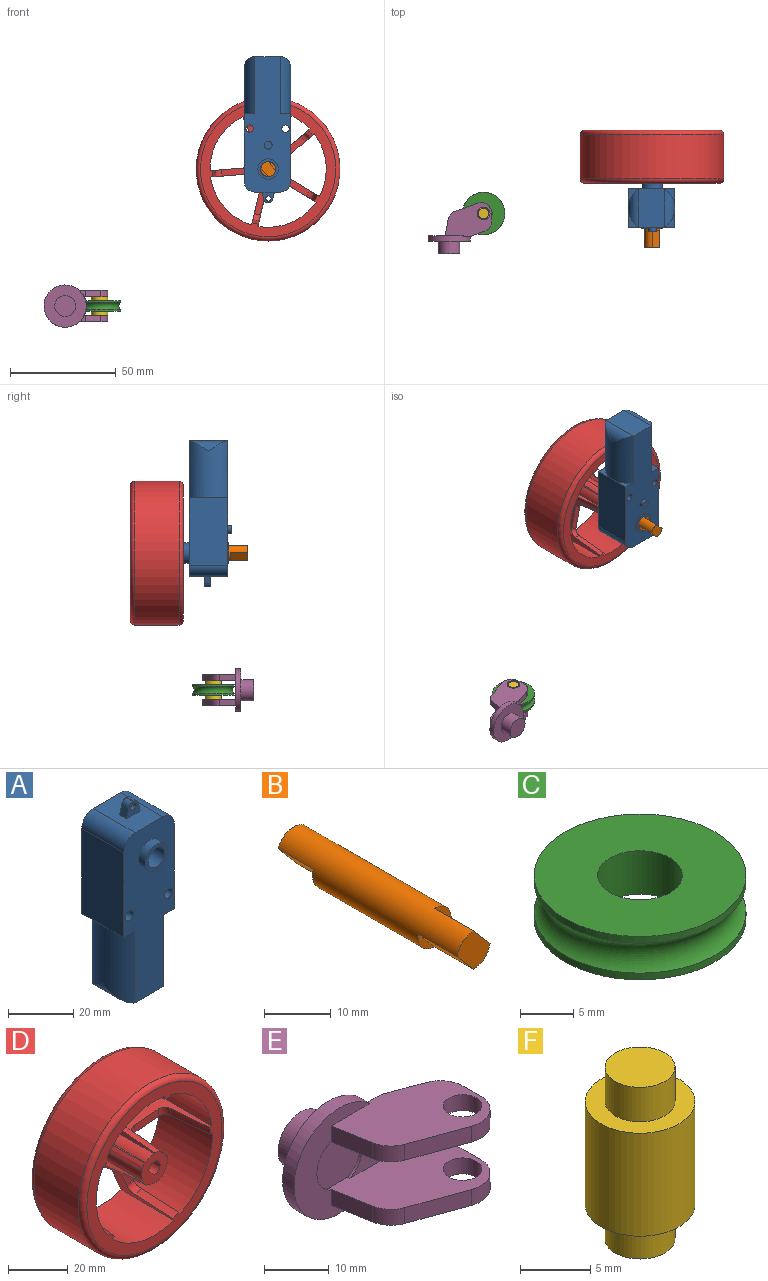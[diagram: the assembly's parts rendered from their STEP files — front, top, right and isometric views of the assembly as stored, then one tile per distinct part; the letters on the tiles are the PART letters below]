
ASSEMBLY  parts=6 mates=4
PART A: 33 faces, bbox 22x23.2x69.1 mm
  f0: plane 32x18.25mm, normal (-1,0,0), area 584mm2, adj f4,f5,f7,f25,f26
  f1: cylinder r=5mm len=18.25mm, axis (0,1,0), area 81.4mm2, adj f4,f5,f8,f24
  f2: cylinder r=5mm len=18.25mm, axis (0,1,0), area 81.4mm2, adj f4,f5,f8,f22
  f3: plane 32x18.25mm, normal (1,0,0), area 584mm2, adj f4,f5,f9,f21,f23
  f4: plane 64x22mm, normal (0,-1,0), area 1041.8mm2, adj f0,f1,f2,f3,f6,f7,f8,f9
  f5: plane 64x22mm, normal (0,1,0), area 1031.1mm2, adj f0,f1,f2,f3,f6,f7,f8,f9
  f6: plane 18.25x12mm, normal (0,0,1), area 201mm2, adj f4,f5,f7,f9,f13,f14,f15,f16
  f7: cylinder r=5mm len=18.25mm, axis (0,1,0), area 143.3mm2, adj f0,f4,f5,f6
  f8: plane 18.25x12mm, normal (0,0,-1), area 219mm2, adj f1,f2,f4,f5
  f9: cylinder r=5mm len=18.25mm, axis (0,1,0), area 143.3mm2, adj f3,f4,f5,f6
  f10: cylinder r=4.85mm len=9.7mm, axis (0,1,0), area 88.4mm2, adj f4,f12
  f11: cylinder r=3.6mm len=21.65mm, axis (0,1,0), area 489.7mm2, adj f12,f28
  f12: plane 9.7x9.7mm, normal (0,-1,0), area 33.2mm2, adj f10,f11
  f13: plane 6x5.1mm, normal (0,-1,0), area 17.8mm2, adj f6,f14,f16,f17,f18,f19,f20
  f14: plane 3.62x3mm, normal (0.97,0,0.26), area 11.2mm2, adj f6,f13,f15,f18
  f15: plane 6x5.1mm, normal (0,1,0), area 17.8mm2, adj f6,f14,f16,f17,f18,f19,f20
  f16: plane 3.62x3mm, normal (-0.97,0,0.26), area 11.2mm2, adj f6,f13,f15,f19
  f17: plane 3x0.2mm, normal (0,0,1), area 0.6mm2, adj f13,f15,f18,f19
  f18: cylinder r=2mm len=3mm, axis (0,1,0), area 7.9mm2, adj f13,f14,f15,f17
  f19: cylinder r=2mm len=3mm, axis (0,1,0), area 7.9mm2, adj f13,f15,f16,f17
  f20: cylinder r=1.25mm len=3mm, axis (0,-1,0), area 23.6mm2, adj f13,f15
  f21: plane 9.13x4.86mm, normal (0,0,-1), area 13.2mm2, adj f3,f5,f22
  f22: cylinder r=11mm len=27mm, axis (0,0,-1), area 539.6mm2, adj f2,f4,f5,f21,f23
  f23: plane 9.13x4.86mm, normal (0,0,-1), area 13.2mm2, adj f3,f4,f22
  f24: cylinder r=11mm len=27mm, axis (0,0,-1), area 539.6mm2, adj f1,f4,f5,f25,f26
  f25: plane 9.13x4.86mm, normal (0,0,-1), area 13.2mm2, adj f0,f5,f24
  f26: plane 9.13x4.86mm, normal (0,0,-1), area 13.2mm2, adj f0,f4,f24
  f27: cylinder r=4.85mm len=9.7mm, axis (0,-1,0), area 15.2mm2, adj f5,f28
  f28: plane 9.7x9.7mm, normal (0,1,0), area 33.2mm2, adj f11,f27
  f29: cylinder r=1.85mm len=3.7mm, axis (0,-1,0), area 23.2mm2, adj f5,f30
  f30: plane 3.7x3.7mm, normal (0,1,0), area 10.8mm2, adj f29
  f31: cylinder r=1.75mm len=18.25mm, axis (0,-1,0), area 200.7mm2, adj f4,f5
  f32: cylinder r=1.75mm len=18.25mm, axis (0,-1,0), area 200.7mm2, adj f4,f5
PART B: 9 faces, bbox 7x38x7 mm
  f0: plane 7x6.93mm, normal (0,-1,0), area 29.7mm2, adj f2,f5,f7
  f1: plane 6.94x6.8mm, normal (0,1,0), area 31mm2, adj f2,f3
  f2: cylinder r=3.5mm len=38mm, axis (0,1,0), area 682.1mm2, adj f0,f1,f3,f4,f5,f6,f7,f8
  f3: plane 7.5x4.6mm, normal (-0.76,0,-0.65), area 45.5mm2, adj f1,f2,f4
  f4: plane 4.66x4.15mm, normal (0,1,0), area 7.5mm2, adj f2,f3
  f5: plane 8.25x4mm, normal (-0.76,0,-0.65), area 43.5mm2, adj f0,f2,f6
  f6: plane 4x3.47mm, normal (0,-1,0), area 4.4mm2, adj f2,f5
  f7: plane 8.25x4mm, normal (0.76,0,0.65), area 43.5mm2, adj f0,f2,f8
  f8: plane 4x3.47mm, normal (0,-1,0), area 4.4mm2, adj f2,f7
PART C: 6 faces, bbox 23.8x23.8x5 mm
  f0: cylinder r=10mm len=20mm, axis (0,0,-1), area 48.3mm2, adj f3,f5
  f1: cylinder r=4mm len=8mm, axis (0,0,-1), area 125.7mm2, adj f3,f4
  f2: cylinder r=10mm len=20mm, axis (0,0,-1), area 48.3mm2, adj f4,f5
  f3: plane 20x20mm, normal (0,0,1), area 263.9mm2, adj f0,f1
  f4: plane 20x20mm, normal (0,0,-1), area 263.9mm2, adj f1,f2
  f5: torus R=11mm, axis (0,0,1), area 246mm2, adj f0,f2
PART D: 53 faces, bbox 73.4x25x73.4 mm
  f0: plane 12.54x12.32mm, normal (0,-1,0), area 97.4mm2, adj f9,f10,f11,f12,f13,f14,f15,f16
  f1: cylinder r=27.5mm len=29.75mm, axis (0,1,0), area 788.9mm2, adj f7,f8,f9,f22
  f2: cylinder r=27.5mm len=29.05mm, axis (0,1,0), area 788.9mm2, adj f7,f8,f10,f12
  f3: cylinder r=27.5mm len=25.5mm, axis (0,1,0), area 788.9mm2, adj f7,f8,f13,f15
  f4: cylinder r=27.5mm len=25mm, axis (0,1,0), area 788.9mm2, adj f7,f8,f16,f18
  f5: cylinder r=27.5mm len=27.55mm, axis (0,1,0), area 788.9mm2, adj f7,f8,f19,f21
  f6: cylinder r=34mm len=68mm, axis (0,1,0), area 4486.2mm2, adj f51,f52
  f7: plane 64x64mm, normal (0,-1,0), area 856.8mm2, adj f1,f2,f3,f4,f5,f9,f10,f12
  f8: plane 64x64mm, normal (0,1,0), area 1257.1mm2, adj f1,f2,f3,f4,f5,f9,f10,f11
  f9: plane 25.04x16.46mm, normal (-0.65,0,0.76), area 174.1mm2, adj f0,f1,f7,f8,f25,f46,f47,f48
  f10: plane 25.04x16.46mm, normal (0.65,0,-0.76), area 174.1mm2, adj f0,f2,f7,f8,f11,f46,f47,f48
  f11: cylinder r=6mm len=25mm, axis (0,1,0), area 112.7mm2, adj f0,f8,f10,f12
  f12: plane 25.04x20.01mm, normal (-0.92,0,-0.39), area 174.1mm2, adj f0,f2,f7,f8,f11,f41,f42,f43
  f13: plane 25.04x20.01mm, normal (0.92,0,0.39), area 174.1mm2, adj f0,f3,f7,f8,f14,f41,f42,f43
  f14: cylinder r=6mm len=25mm, axis (0,1,0), area 112.7mm2, adj f0,f8,f13,f15
  f15: plane 25.04x21.61mm, normal (0.08,0,-1), area 174.1mm2, adj f0,f3,f7,f8,f14,f36,f37,f38
  f16: plane 25.04x21.61mm, normal (-0.08,0,1), area 174.1mm2, adj f0,f4,f7,f8,f17,f36,f37,f38
  f17: cylinder r=6mm len=25mm, axis (0,1,0), area 112.7mm2, adj f0,f8,f16,f18
  f18: plane 25.04x21.1mm, normal (0.97,0,-0.23), area 174.1mm2, adj f0,f4,f7,f8,f17,f31,f32,f33
  f19: plane 25.04x21.1mm, normal (-0.97,0,0.23), area 174.1mm2, adj f0,f5,f7,f8,f20,f31,f32,f33
  f20: cylinder r=6mm len=25mm, axis (0,1,0), area 112.7mm2, adj f0,f8,f19,f21
  f21: plane 25.04x18.53mm, normal (0.52,0,0.85), area 174.1mm2, adj f0,f5,f7,f8,f20,f26,f27,f28
  f22: plane 25.04x18.53mm, normal (-0.52,0,-0.85), area 174.1mm2, adj f0,f1,f7,f8,f25,f26,f27,f28
  f23: cylinder r=2.7mm len=25mm, axis (0,1,0), area 310.6mm2, adj f0,f8,f24
  f24: plane 25x3.05mm, normal (0.76,0,0.65), area 100.6mm2, adj f0,f8,f23
  f25: cylinder r=6mm len=25mm, axis (0,1,0), area 112.7mm2, adj f0,f8,f9,f22
  f26: cone r=26.46mm half-angle=5deg, axis (0,-1,0), area 52mm2, adj f7,f21,f22,f27
  f27: torus R=21.96mm, axis (0,-1,0), area 13.4mm2, adj f21,f22,f26,f28
  f28: plane 11.13x8.39mm, normal (0,-1,0), area 33.5mm2, adj f21,f22,f27,f29
  f29: torus R=10.81mm, axis (0,-1,0), area 13.4mm2, adj f21,f22,f28,f30
  f30: cone r=7.82mm half-angle=5deg, axis (0,1,0), area 52.8mm2, adj f0,f21,f22,f29
  f31: cone r=26.46mm half-angle=5deg, axis (0,-1,0), area 52mm2, adj f7,f18,f19,f32
  f32: torus R=21.96mm, axis (0,-1,0), area 13.4mm2, adj f18,f19,f31,f33
  f33: plane 11.6x5.5mm, normal (0,-1,0), area 33.5mm2, adj f18,f19,f32,f34
  f34: torus R=10.81mm, axis (0,-1,0), area 13.4mm2, adj f18,f19,f33,f35
  f35: cone r=7.82mm half-angle=5deg, axis (0,1,0), area 52.8mm2, adj f0,f18,f19,f34
  f36: cone r=26.46mm half-angle=5deg, axis (0,-1,0), area 52mm2, adj f7,f15,f16,f37
  f37: torus R=21.96mm, axis (0,-1,0), area 13.4mm2, adj f15,f16,f36,f38
  f38: plane 11.41x3.9mm, normal (0,-1,0), area 33.5mm2, adj f15,f16,f37,f39
  f39: torus R=10.81mm, axis (0,-1,0), area 13.4mm2, adj f15,f16,f38,f40
  f40: cone r=7.82mm half-angle=5deg, axis (0,1,0), area 52.8mm2, adj f0,f15,f16,f39
  f41: cone r=26.46mm half-angle=5deg, axis (0,-1,0), area 52mm2, adj f7,f12,f13,f42
  f42: torus R=21.96mm, axis (0,-1,0), area 13.4mm2, adj f12,f13,f41,f43
  f43: plane 11.5x7.09mm, normal (0,-1,0), area 33.5mm2, adj f12,f13,f42,f44
  f44: torus R=10.81mm, axis (0,-1,0), area 13.4mm2, adj f12,f13,f43,f45
  f45: cone r=7.82mm half-angle=5deg, axis (0,1,0), area 52.8mm2, adj f0,f12,f13,f44
  f46: cone r=7.82mm half-angle=5deg, axis (0,1,0), area 52.8mm2, adj f0,f9,f10,f47
  f47: torus R=10.81mm, axis (0,-1,0), area 13.4mm2, adj f9,f10,f46,f48
  f48: plane 10.46x9.58mm, normal (0,-1,0), area 33.5mm2, adj f9,f10,f47,f49
  f49: torus R=21.96mm, axis (0,-1,0), area 13.4mm2, adj f9,f10,f48,f50
  f50: cone r=26.46mm half-angle=5deg, axis (0,-1,0), area 52mm2, adj f7,f9,f10,f49
  f51: torus R=32mm, axis (0,-1,0), area 656.8mm2, adj f6,f8
  f52: torus R=32mm, axis (0,-1,0), area 656.8mm2, adj f6,f7
PART E: 31 faces, bbox 30.1x24.2x20 mm
  f0: cylinder r=5mm len=9mm, axis (0,-1,0), area 5.6mm2, adj f4,f11,f16,f20
  f1: cylinder r=5mm len=9.25mm, axis (0,-1,0), area 5.9mm2, adj f2,f6,f16,f22
  f2: plane 20x16.61mm, normal (0,-1,0), area 130.5mm2, adj f1,f3,f6,f12,f19,f22
  f3: plane 22.02x16.2mm, normal (0,0,1), area 238mm2, adj f2,f5,f6,f7,f8,f9,f10,f12
  f4: plane 22.11x16.2mm, normal (0,0,-1), area 238.9mm2, adj f0,f5,f6,f7,f8,f9,f10,f11
  f5: plane 3x2.96mm, normal (0,1,0), area 4.9mm2, adj f3,f4,f10,f12
  f6: plane 8.22x3mm, normal (-0.98,-0.18,0), area 23.6mm2, adj f1,f2,f3,f4,f16,f17
  f7: plane 10.71x3.86mm, normal (-0.34,-0.94,0), area 34.2mm2, adj f3,f4,f17,f30
  f8: plane 3.77x3mm, normal (1,0,0), area 11.3mm2, adj f3,f4,f18,f30
  f9: cylinder r=3mm len=6mm, axis (0,0,-1), area 56.5mm2, adj f3,f4
  f10: plane 7.31x3mm, normal (0.35,0.94,0), area 23.4mm2, adj f3,f4,f5,f18
  f11: plane 9x7.82mm, normal (0,-1,0), area 49.1mm2, adj f0,f4,f12,f20
  f12: cylinder r=10mm len=20mm, axis (0,-1,0), area 153.3mm2, adj f2,f3,f4,f5,f11,f13,f19,f20
  f13: plane 20x20mm, normal (0,1,0), area 235.6mm2, adj f12,f15
  f14: plane 10x10mm, normal (0,1,0), area 78.5mm2, adj f15
  f15: cylinder r=5mm len=10mm, axis (0,-1,0), area 188.5mm2, adj f13,f14
  f16: plane 10x9.18mm, normal (0,-1,0), area 75.6mm2, adj f0,f1,f4,f6,f20,f22
  f17: cylinder r=5mm len=3.82mm, axis (0,0,1), area 15.7mm2, adj f3,f4,f6,f7
  f18: cylinder r=5mm len=4.68mm, axis (0,0,1), area 18.2mm2, adj f3,f4,f8,f10
  f19: plane 22.02x16.2mm, normal (0,0,-1), area 238mm2, adj f2,f12,f21,f22,f23,f24,f25,f26
  f20: plane 22.11x16.2mm, normal (0,0,1), area 238.9mm2, adj f0,f11,f12,f16,f21,f22,f23,f24
  f21: plane 3x2.96mm, normal (0,1,0), area 4.9mm2, adj f12,f19,f20,f26
  f22: plane 8.22x3mm, normal (-0.98,-0.18,0), area 23.6mm2, adj f1,f2,f16,f19,f20,f27
  f23: plane 10.71x3.86mm, normal (-0.34,-0.94,0), area 34.2mm2, adj f19,f20,f27,f29
  f24: plane 3.77x3mm, normal (1,0,0), area 11.3mm2, adj f19,f20,f28,f29
  f25: cylinder r=3mm len=6mm, axis (0,0,1), area 56.5mm2, adj f19,f20
  f26: plane 7.31x3mm, normal (0.35,0.94,0), area 23.4mm2, adj f19,f20,f21,f28
  f27: cylinder r=5mm len=3.82mm, axis (0,0,-1), area 15.7mm2, adj f19,f20,f22,f23
  f28: cylinder r=5mm len=4.68mm, axis (0,0,-1), area 18.2mm2, adj f19,f20,f24,f26
  f29: cylinder r=5mm len=6.7mm, axis (0,0,1), area 28.7mm2, adj f19,f20,f23,f24
  f30: cylinder r=5mm len=6.7mm, axis (0,0,-1), area 28.7mm2, adj f3,f4,f7,f8
PART F: 7 faces, bbox 7.9x7.9x15 mm
  f0: cylinder r=3.92mm len=9mm, axis (0,0,1), area 222mm2, adj f1,f2
  f1: plane 7.85x7.85mm, normal (0,0,-1), area 28.8mm2, adj f0,f5
  f2: plane 7.85x7.85mm, normal (0,0,1), area 28.8mm2, adj f0,f4
  f3: plane 5x5mm, normal (0,0,1), area 19.6mm2, adj f4
  f4: cylinder r=2.5mm len=5mm, axis (0,0,1), area 47.1mm2, adj f2,f3
  f5: cylinder r=2.5mm len=5mm, axis (0,0,1), area 47.1mm2, adj f1,f6
  f6: plane 5x5mm, normal (0,0,-1), area 19.6mm2, adj f5
PLACE A rot(axis=(1,0,0),180deg) t=(101.99,140.12,106.3)mm fixed
PLACE B rot(axis=(0,1,0),180deg) t=(229.15,-84.6,106.3)mm
PLACE C rot(axis=(1,0,0),180deg) t=(85.84,24.62,-17.2)mm
PLACE D rot(axis=(0,1,0),180deg) t=(229.15,-84.6,106.3)mm
PLACE E rot(axis=(1,0,0),180deg) t=(85.84,24.62,-17.2)mm
PLACE F t=(85.84,24.62,-22.2)mm
MATE revolute A.f10 <-> B.f2  axis (0,-1,0) through (165.57,17.35,45.12)mm
MATE fastened D.f24 <-> B.f3  axis (-0.76,0,-0.65) through (166.9,38.85,46.26)mm
MATE revolute E.f9 <-> F.f4  axis (0,0,-1) through (85.84,24.62,-15.2)mm
MATE fastened C.f1 <-> F.f0  axis (0,0,1) through (85.84,24.62,-19.7)mm
